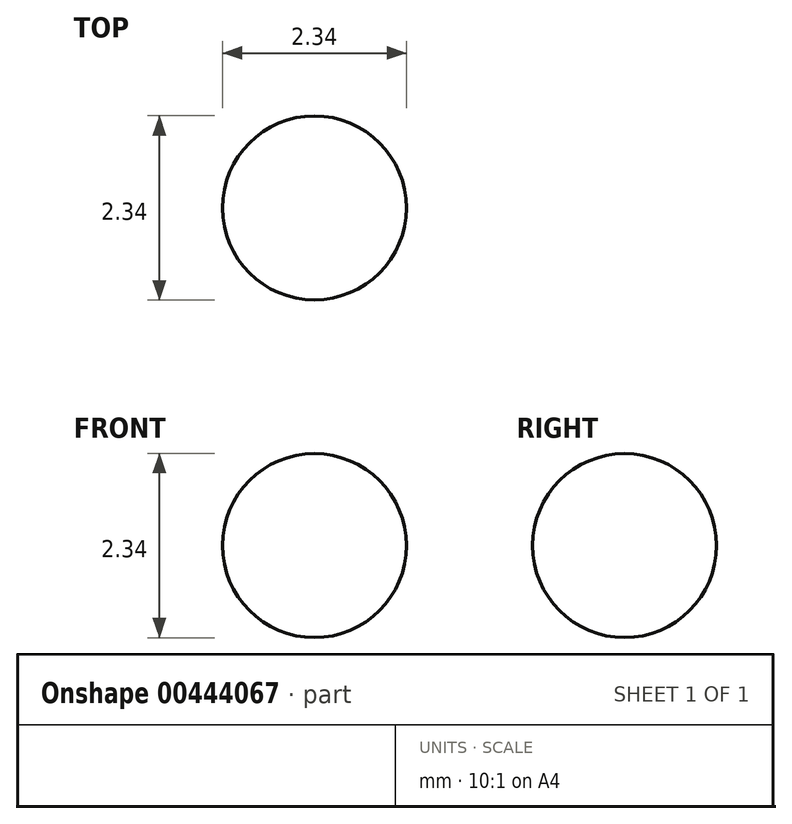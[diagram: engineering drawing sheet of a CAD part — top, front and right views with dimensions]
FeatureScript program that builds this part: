
annotation { "Feature Type Name" : "Feature", "Feature Type Description" : "" }
export const myFeature = defineFeature(function(context is Context, id is Id, definition is map)
    precondition{}
    {
        {
            var Q0;
            Q0=qCreatedBy(makeId("Front.planeOp"),FACE);
            var sketch = newSketch(context, id + "F0", { "sketchPlane" : qUnion([Q0])});
            skCircle(sketch, "E0", {"center": v(0, 0) * mm, "radius": 1.17 * mm});
            skLineSegment(sketch, "E1", {"start": v(0, 1.17) * mm, "end": v(0, -1.17) * mm});
            skSolve(sketch);
        }
        {
            var Q0;
            {var subQ0=sQuery(id+"F0.wireOp",EDGE,"E1");Q0=makeQuery(id+"F0.imprint","IMPRINT",FACE,{"disambiguationData":[TD([[makeQuery(id+"F0.imprint","IMPRINT",EDGE,{"derivedFrom":subQ0}),-1.0]])]});}
            var Q1;
            Q1=sQuery(id+"F0.wireOp",EDGE,"E1");
            revolve(context, id + "F1", {"entities" : qUnion([Q0]), "axis" : qUnion([Q1]), "revolveType" : RevolveType.FULL});
        }
    });
